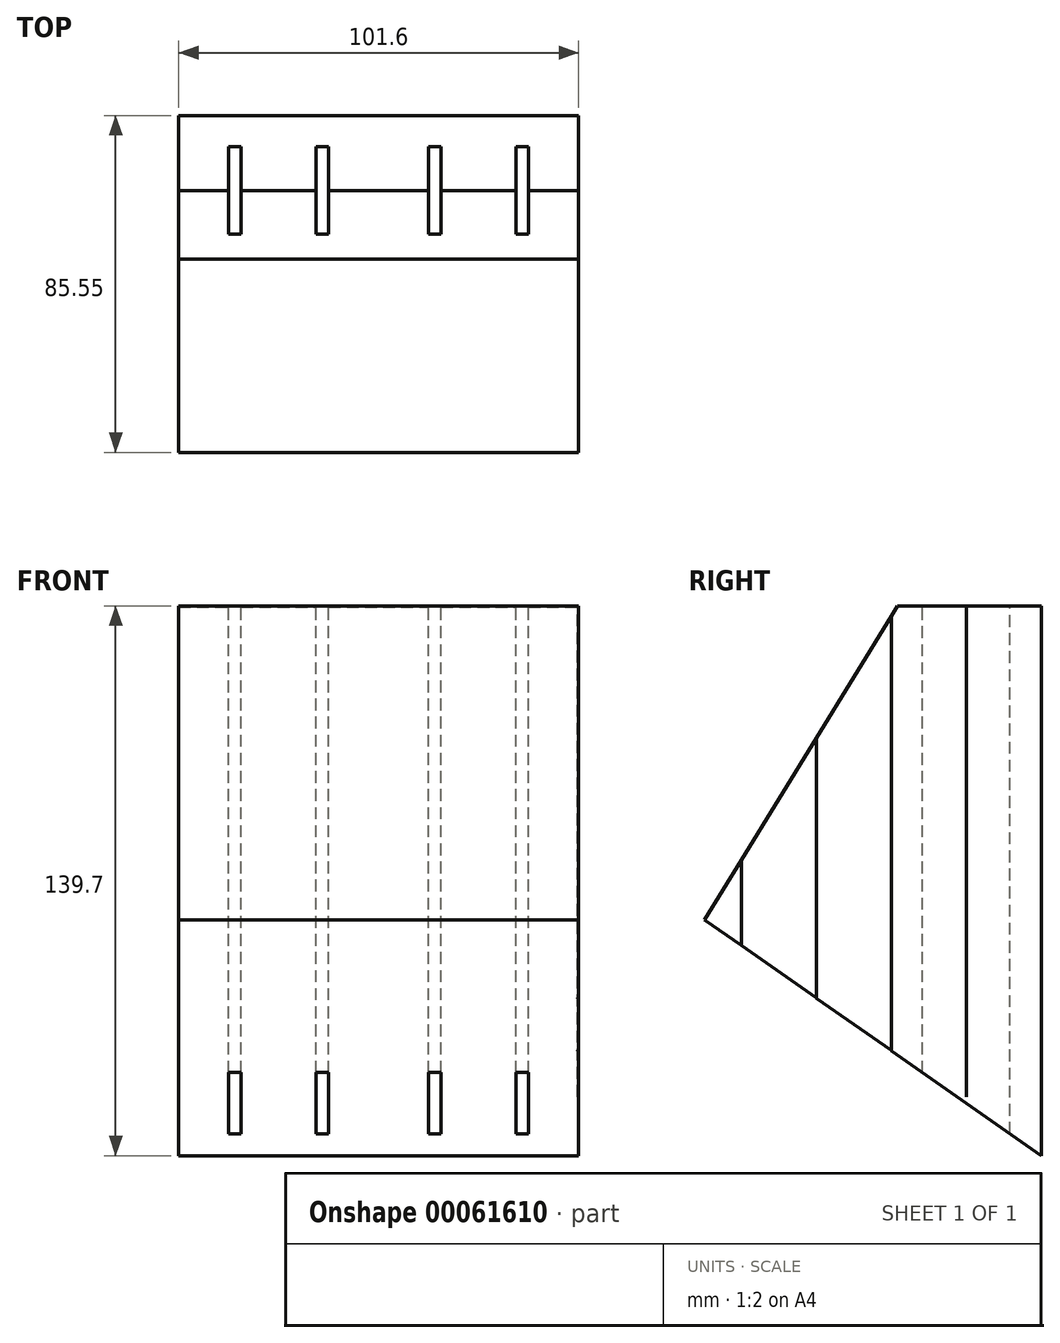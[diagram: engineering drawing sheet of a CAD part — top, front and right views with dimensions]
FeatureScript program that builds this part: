
annotation { "Feature Type Name" : "Feature", "Feature Type Description" : "" }
export const myFeature = defineFeature(function(context is Context, id is Id, definition is map)
    precondition{}
    {
        {
            var Q0;
            Q0=qCreatedBy(makeId("Right.planeOp"),FACE);
            var sketch = newSketch(context, id + "F0", { "sketchPlane" : qUnion([Q0])});
            skLineSegment(sketch, "E0", {"start": v(0, 0) * mm, "end": v(-95.25, 0) * mm});
            skLineSegment(sketch, "E1", {"start": v(0, 0) * mm, "end": v(0, -139.7) * mm});
            skLineSegment(sketch, "E2", {"start": v(0, -139.7) * mm, "end": v(-95.25, -73) * mm});
            skLineSegment(sketch, "E3", {"start": v(-95.25, -73) * mm, "end": v(-95.25, 0) * mm});
            skSolve(sketch);
        }
        {
            var Q0;
            Q0 = qSketchRegion(id + "F0", true);
            extrude(context, id + "F1", {"entities" : qUnion([Q0]), "endBound" : BoundingType.SYMMETRIC, "depth" : 101.6 * mm});
        }
        {
            var Q0;
            Q0=makeQuery(id+"F1.opExtrude","SWEPT_FACE",FACE,{"disambiguationData":[OSD([sQuery(id+"F0.wireOp",EDGE,"E0")])]});
            var sketch = newSketch(context, id + "F2", { "sketchPlane" : qUnion([Q0])});
            skLineSegment(sketch, "E4.bottom", {"start": v(-38.1, -30.16) * mm, "end": v(-34.93, -30.16) * mm});
            skLineSegment(sketch, "E4.top", {"start": v(-38.1, -7.94) * mm, "end": v(-34.93, -7.94) * mm});
            skLineSegment(sketch, "E4.left", {"start": v(-38.1, -30.16) * mm, "end": v(-38.1, -7.94) * mm});
            skLineSegment(sketch, "E4.right", {"start": v(-34.93, -30.16) * mm, "end": v(-34.93, -7.94) * mm});
            skLineSegment(sketch, "E5.bottom", {"start": v(-15.88, -30.16) * mm, "end": v(-12.7, -30.16) * mm});
            skLineSegment(sketch, "E5.top", {"start": v(-15.88, -7.94) * mm, "end": v(-12.7, -7.94) * mm});
            skLineSegment(sketch, "E5.left", {"start": v(-15.87, -30.16) * mm, "end": v(-15.88, -7.94) * mm});
            skLineSegment(sketch, "E5.right", {"start": v(-12.7, -30.16) * mm, "end": v(-12.7, -7.94) * mm});
            skLineSegment(sketch, "E6.bottom", {"start": v(12.7, -30.16) * mm, "end": v(15.88, -30.16) * mm});
            skLineSegment(sketch, "E6.top", {"start": v(12.7, -7.94) * mm, "end": v(15.88, -7.94) * mm});
            skLineSegment(sketch, "E6.left", {"start": v(12.7, -30.16) * mm, "end": v(12.7, -7.94) * mm});
            skLineSegment(sketch, "E6.right", {"start": v(15.88, -30.16) * mm, "end": v(15.87, -7.94) * mm});
            skLineSegment(sketch, "E7.bottom", {"start": v(34.93, -30.16) * mm, "end": v(38.1, -30.16) * mm});
            skLineSegment(sketch, "E7.top", {"start": v(34.93, -7.94) * mm, "end": v(38.1, -7.94) * mm});
            skLineSegment(sketch, "E7.left", {"start": v(34.93, -30.16) * mm, "end": v(34.93, -7.94) * mm});
            skLineSegment(sketch, "E7.right", {"start": v(38.1, -30.16) * mm, "end": v(38.1, -7.94) * mm});
            skLineSegment(sketch, "E8", {"start": v(0, 0) * mm, "end": v(0, 30.95) * mm, "construction": true});
            skSolve(sketch);
        }
        {
            var Q0;
            Q0 = qSketchRegion(id + "F2", true);
            var Q1;
            Q1=makeQuery(id+"F1.opExtrude","SWEPT_FACE",FACE,{"disambiguationData":[OSD([sQuery(id+"F0.wireOp",EDGE,"E2")])]});
            extrude(context, id + "F3", {"entities" : qUnion([Q0]), "operationType" : NewBodyOperationType.REMOVE, "endBound" : BoundingType.UP_TO_SURFACE, "oppositeDirection" : true, "endBoundEntityFace" : qUnion([Q1]), "depth" : 25.4 * mm});
        }
        {
            var Q0;
            Q0=makeQuery(id+"F1.opExtrude","SWEPT_FACE",FACE,{"disambiguationData":[OSD([sQuery(id+"F0.wireOp",EDGE,"E0")])]});
            var sketch = newSketch(context, id + "F4", { "sketchPlane" : qUnion([Q0])});
            skCircle(sketch, "E9", {"center": v(0, -57.15) * mm, "radius": 9.53 * mm});
            skSolve(sketch);
        }
        {
            var Q0;
            Q0=makeQuery(id+"F1.opExtrude","SWEPT_FACE",FACE,{"disambiguationData":[OSD([sQuery(id+"F0.wireOp",EDGE,"E0")])]});
            var sketch = newSketch(context, id + "F5", { "sketchPlane" : qUnion([Q0])});
            skLineSegment(sketch, "E10.bottom", {"start": v(-50.8, -19.08) * mm, "end": v(50.8, -19.08) * mm});
            skLineSegment(sketch, "E10.top", {"start": v(-50.8, -19.05) * mm, "end": v(50.8, -19.05) * mm});
            skLineSegment(sketch, "E10.left", {"start": v(-50.8, -19.08) * mm, "end": v(-50.8, -19.05) * mm});
            skLineSegment(sketch, "E10.right", {"start": v(50.8, -19.08) * mm, "end": v(50.8, -19.05) * mm});
            skLineSegment(sketch, "E11.bottom", {"start": v(-50.8, -38.13) * mm, "end": v(50.8, -38.13) * mm});
            skLineSegment(sketch, "E11.top", {"start": v(-50.8, -38.1) * mm, "end": v(50.8, -38.1) * mm});
            skLineSegment(sketch, "E11.left", {"start": v(-50.8, -38.13) * mm, "end": v(-50.8, -38.1) * mm});
            skLineSegment(sketch, "E11.right", {"start": v(50.8, -38.13) * mm, "end": v(50.8, -38.1) * mm});
            skLineSegment(sketch, "E12.bottom", {"start": v(50.8, -57.15) * mm, "end": v(-50.8, -57.15) * mm});
            skLineSegment(sketch, "E12.top", {"start": v(50.8, -57.18) * mm, "end": v(-50.8, -57.18) * mm});
            skLineSegment(sketch, "E12.left", {"start": v(50.8, -57.18) * mm, "end": v(50.8, -57.15) * mm});
            skLineSegment(sketch, "E12.right", {"start": v(-50.8, -57.18) * mm, "end": v(-50.8, -57.15) * mm});
            skSolve(sketch);
        }
        {
            var Q0;
            Q0 = qSketchRegion(id + "F5", true);
            extrude(context, id + "F6", {"entities" : qUnion([Q0]), "operationType" : NewBodyOperationType.REMOVE, "oppositeDirection" : true, "depth" : 0.25 * mm});
        }
        {
            var Q0;
            Q0=makeQuery(id+"F1.opExtrude","CAP_FACE",FACE,{"disambiguationData":[OSD([sQuery(id+"F0.wireOp",EDGE,"E0"),sQuery(id+"F0.wireOp",EDGE,"E1"),sQuery(id+"F0.wireOp",EDGE,"E2"),sQuery(id+"F0.wireOp",EDGE,"E3")])],"isStart":false});
            var sketch = newSketch(context, id + "F7", { "sketchPlane" : qUnion([Q0])});
            skLineSegment(sketch, "E13.0", {"start": v(-85.55, -79.8) * mm, "end": v(-36.51, 0) * mm});
            skLineSegment(sketch, "E14", {"start": v(-85.55, -79.8) * mm, "end": v(-105.28, -79.8) * mm});
            skLineSegment(sketch, "E15", {"start": v(-105.28, -79.8) * mm, "end": v(-105.28, 0) * mm});
            skLineSegment(sketch, "E16", {"start": v(-105.28, 0) * mm, "end": v(-36.51, 0) * mm});
            skSolve(sketch);
        }
        {
            var Q0;
            Q0 = qSketchRegion(id + "F7", true);
            extrude(context, id + "F8", {"entities" : qUnion([Q0]), "operationType" : NewBodyOperationType.REMOVE, "endBound" : BoundingType.THROUGH_ALL, "oppositeDirection" : true, "depth" : 25.4 * mm});
        }
        {
            var Q0;
            Q0=makeQuery(id+"F1.opExtrude","CAP_FACE",FACE,{"disambiguationData":[OSD([sQuery(id+"F0.wireOp",EDGE,"E0"),sQuery(id+"F0.wireOp",EDGE,"E1"),sQuery(id+"F0.wireOp",EDGE,"E2"),sQuery(id+"F0.wireOp",EDGE,"E3")])],"isStart":false});
            var sketch = newSketch(context, id + "F9", { "sketchPlane" : qUnion([Q0])});
            skLineSegment(sketch, "E17.bottom", {"start": v(-19.05, 0) * mm, "end": v(-19.08, 0) * mm});
            skLineSegment(sketch, "E17.top", {"start": v(-19.05, -124.75) * mm, "end": v(-19.08, -124.75) * mm});
            skLineSegment(sketch, "E17.left", {"start": v(-19.05, 0) * mm, "end": v(-19.05, -124.75) * mm});
            skLineSegment(sketch, "E17.right", {"start": v(-19.08, 0) * mm, "end": v(-19.08, -124.75) * mm});
            skLineSegment(sketch, "E18.bottom", {"start": v(-38.1, 0) * mm, "end": v(-38.13, 0) * mm});
            skLineSegment(sketch, "E18.top", {"start": v(-38.1, -118.28) * mm, "end": v(-38.13, -118.28) * mm});
            skLineSegment(sketch, "E18.left", {"start": v(-38.1, 0) * mm, "end": v(-38.1, -118.28) * mm});
            skLineSegment(sketch, "E18.right", {"start": v(-38.13, 0) * mm, "end": v(-38.13, -118.28) * mm});
            skLineSegment(sketch, "E19.bottom", {"start": v(-57.15, 0) * mm, "end": v(-57.18, 0) * mm});
            skLineSegment(sketch, "E19.top", {"start": v(-57.15, -108.94) * mm, "end": v(-57.18, -108.94) * mm});
            skLineSegment(sketch, "E19.left", {"start": v(-57.15, 0) * mm, "end": v(-57.15, -108.94) * mm});
            skLineSegment(sketch, "E19.right", {"start": v(-57.18, 0) * mm, "end": v(-57.18, -108.94) * mm});
            skLineSegment(sketch, "E20.bottom", {"start": v(-76.2, 0) * mm, "end": v(-76.23, 0) * mm});
            skLineSegment(sketch, "E20.top", {"start": v(-76.2, -108.23) * mm, "end": v(-76.23, -108.23) * mm});
            skLineSegment(sketch, "E20.left", {"start": v(-76.2, 0) * mm, "end": v(-76.2, -108.23) * mm});
            skLineSegment(sketch, "E20.right", {"start": v(-76.23, 0) * mm, "end": v(-76.23, -108.23) * mm});
            skSolve(sketch);
        }
        {
            var Q0;
            Q0 = qSketchRegion(id + "F9", true);
            extrude(context, id + "F10", {"entities" : qUnion([Q0]), "operationType" : NewBodyOperationType.REMOVE, "oppositeDirection" : true, "depth" : 0.25 * mm});
        }
    });
